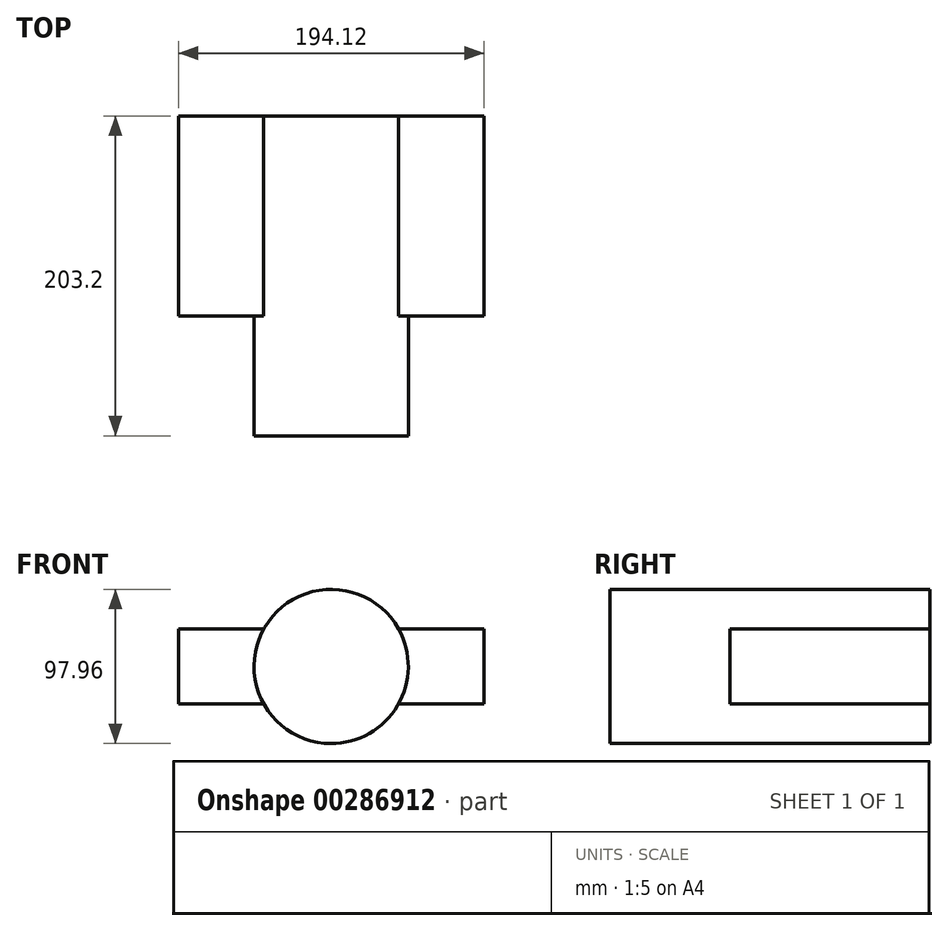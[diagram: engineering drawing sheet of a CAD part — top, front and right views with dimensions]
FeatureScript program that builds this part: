
annotation { "Feature Type Name" : "Feature", "Feature Type Description" : "" }
export const myFeature = defineFeature(function(context is Context, id is Id, definition is map)
    precondition{}
    {
        {
            var Q0;
            Q0=qCreatedBy(makeId("Front.planeOp"),FACE);
            var sketch = newSketch(context, id + "F0", { "sketchPlane" : qUnion([Q0])});
            skCircle(sketch, "E0", {"center": v(0, 0) * mm, "radius": 48.98 * mm});
            skSolve(sketch);
        }
        {
            var Q0;
            Q0 = qSketchRegion(id + "F0", true);
            extrude(context, id + "F1", {"entities" : qUnion([Q0]), "depth" : 203.2 * mm});
        }
        {
            var Q0;
            Q0=qCreatedBy(makeId("Front.planeOp"),FACE);
            var sketch = newSketch(context, id + "F2", { "sketchPlane" : qUnion([Q0])});
            skLineSegment(sketch, "E1.bottom", {"start": v(-97.06, 23.76) * mm, "end": v(97.06, 23.76) * mm});
            skLineSegment(sketch, "E1.top", {"start": v(-97.06, -23.76) * mm, "end": v(97.06, -23.76) * mm});
            skLineSegment(sketch, "E1.left", {"start": v(-97.06, 23.76) * mm, "end": v(-97.06, -23.76) * mm});
            skLineSegment(sketch, "E1.right", {"start": v(97.06, 23.76) * mm, "end": v(97.06, -23.76) * mm});
            skPoint(sketch, "E1.middle", {"position": v(0, 0) * mm});
            skSolve(sketch);
        }
        {
            var Q0;
            Q0 = qSketchRegion(id + "F2", true);
            extrude(context, id + "F3", {"entities" : qUnion([Q0]), "operationType" : NewBodyOperationType.ADD, "depth" : 127 * mm});
        }
    });
